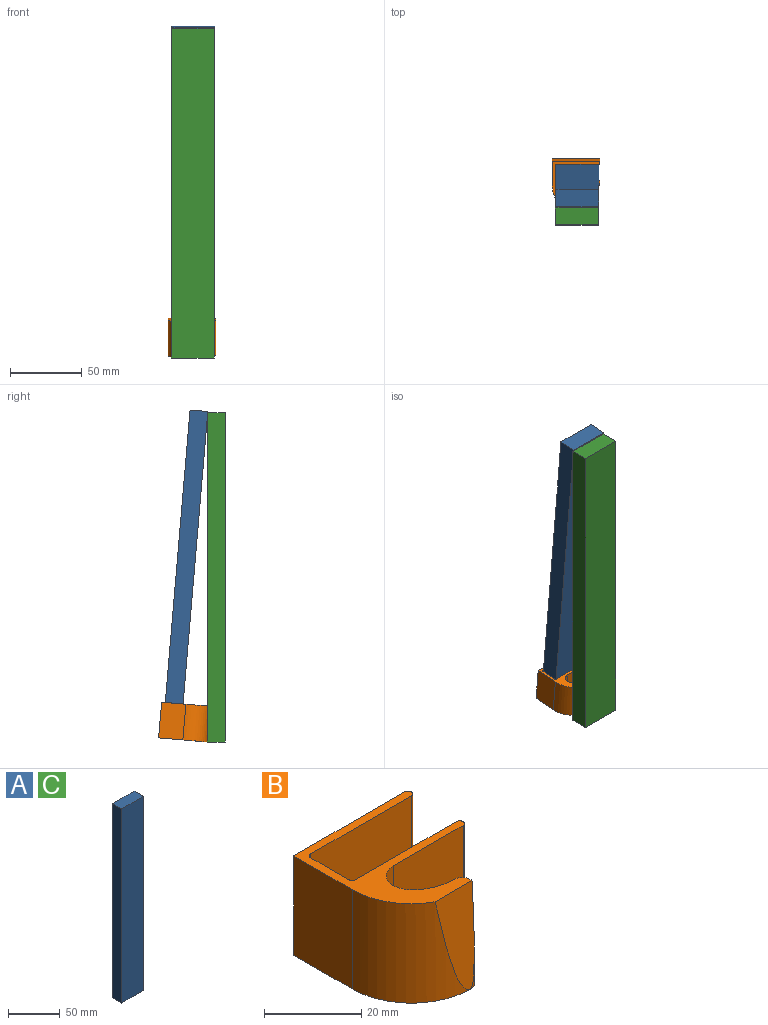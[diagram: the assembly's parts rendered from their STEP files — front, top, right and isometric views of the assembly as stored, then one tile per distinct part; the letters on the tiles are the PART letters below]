
ASSEMBLY  parts=3 mates=2
PART A: 6 faces, bbox 30x12.5x230 mm
  f0: plane 230x12.5mm, normal (1,0,0), area 2875mm2, adj f1,f3,f4,f5
  f1: plane 230x30mm, normal (0,1,0), area 6900mm2, adj f0,f2,f4,f5
  f2: plane 230x12.5mm, normal (-1,0,0), area 2875mm2, adj f1,f3,f4,f5
  f3: plane 230x30mm, normal (0,-1,0), area 6900mm2, adj f0,f2,f4,f5
  f4: plane 30x12.5mm, normal (0,0,1), area 375mm2, adj f0,f1,f2,f3
  f5: plane 30x12.5mm, normal (0,0,-1), area 375mm2, adj f0,f1,f2,f3
PART B: 17 faces, bbox 33.3x34.3x25 mm
  f0: cylinder r=17.25mm len=25mm, axis (0,0,-1), area 534mm2, adj f2,f4,f12,f16
  f1: cylinder r=2.5mm len=25mm, axis (0,0,-1), area 139.4mm2, adj f2,f5,f12,f16
  f2: plane 33.25x32.13mm, normal (0,0,1), area 283.2mm2, adj f0,f1,f3,f4,f5,f6,f7,f8
  f3: plane 32.25x25mm, normal (0,1,0), area 806.3mm2, adj f2,f4,f11,f12
  f4: plane 25x17mm, normal (-1,0,0), area 425mm2, adj f0,f2,f3,f12
  f5: cylinder r=12.25mm len=25mm, axis (0,0,-1), area 248mm2, adj f1,f2,f12,f13
  f6: plane 25x20.25mm, normal (0,-1,0), area 506.3mm2, adj f2,f7,f12,f13
  f7: cylinder r=1mm len=25mm, axis (0,0,-1), area 78.5mm2, adj f2,f6,f8,f12
  f8: plane 29.25x25mm, normal (0,1,0), area 731.3mm2, adj f2,f7,f12,f14
  f9: plane 25x11mm, normal (1,0,0), area 275mm2, adj f2,f12,f14,f15
  f10: plane 29.25x25mm, normal (0,-1,0), area 731.3mm2, adj f2,f11,f12,f15
  f11: cylinder r=1mm len=25mm, axis (0,0,-1), area 78.5mm2, adj f2,f3,f10,f12
  f12: plane 34.25x33.25mm, normal (0,0,-1), area 299.1mm2, adj f0,f1,f3,f4,f5,f6,f7,f8
  f13: cylinder r=5mm len=25mm, axis (0,0,-1), area 291.5mm2, adj f2,f5,f6,f12
  f14: cylinder r=1mm len=25mm, axis (0,0,-1), area 39.3mm2, adj f2,f8,f9,f12
  f15: cylinder r=1mm len=25mm, axis (0,0,1), area 39.3mm2, adj f2,f9,f10,f12
  f16: plane 25x10.76mm, normal (0,-1,0.08), area 187.3mm2, adj f0,f1,f2
PART C: same geometry as A
PLACE A rot(axis=(1,0,0),4.8deg) t=(0.38,31.66,2.15)mm
PLACE B rot(axis=(1,0,0),4.8deg) t=(0,31.91,2.18)mm
PLACE C at identity fixed
MATE fastened B.f16 <-> C.f1  axis (0,-1,0) through (0,6.25,0)mm
MATE fastened A.f3 <-> B.f8  axis (0,-1,-0.08) through (0.38,25.43,1.63)mm
